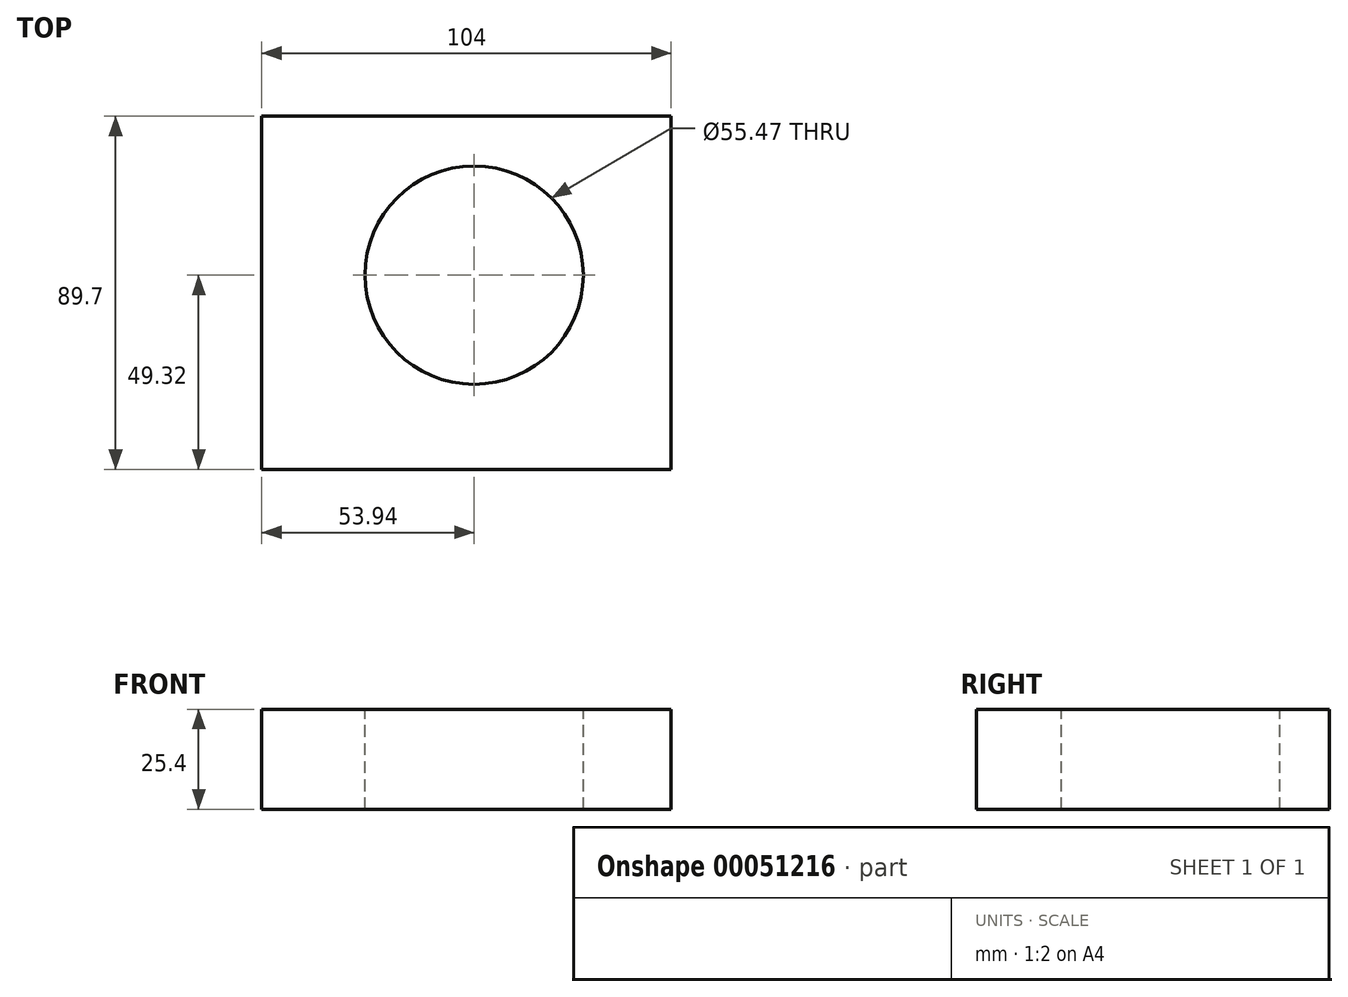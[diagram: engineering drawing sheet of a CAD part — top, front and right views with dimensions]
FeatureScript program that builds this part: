
annotation { "Feature Type Name" : "Feature", "Feature Type Description" : "" }
export const myFeature = defineFeature(function(context is Context, id is Id, definition is map)
    precondition{}
    {
        {
            var Q0;
            Q0=qCreatedBy(makeId("Top.planeOp"),FACE);
            var sketch = newSketch(context, id + "F0", { "sketchPlane" : qUnion([Q0])});
            skLineSegment(sketch, "E0.bottom", {"start": v(-53.94, 40.38) * mm, "end": v(50.06, 40.38) * mm});
            skLineSegment(sketch, "E0.top", {"start": v(-53.94, -49.32) * mm, "end": v(50.06, -49.32) * mm});
            skLineSegment(sketch, "E0.left", {"start": v(-53.94, 40.38) * mm, "end": v(-53.94, -49.32) * mm});
            skLineSegment(sketch, "E0.right", {"start": v(50.06, 40.38) * mm, "end": v(50.06, -49.32) * mm});
            skSolve(sketch);
        }
        {
            var Q0;
            Q0=makeQuery(id+"F0.imprint","IMPRINT",FACE,{"disambiguationData":[TD([[makeQuery(id+"F0.imprint","IMPRINT",EDGE,{"derivedFrom":sQuery(id+"F0.wireOp",EDGE,"E0.bottom")}),-1.0]])]});
            extrude(context, id + "F1", {"entities" : qUnion([Q0]), "depth" : 25.4 * mm});
        }
        {
            var Q0;
            Q0=makeQuery(id+"F1.opExtrude","CAP_FACE",FACE,{"disambiguationData":[OSD([sQuery(id+"F0.wireOp",EDGE,"E0.bottom"),sQuery(id+"F0.wireOp",EDGE,"E0.top"),sQuery(id+"F0.wireOp",EDGE,"E0.left"),sQuery(id+"F0.wireOp",EDGE,"E0.right")])],"isStart":false});
            var sketch = newSketch(context, id + "F2", { "sketchPlane" : qUnion([Q0])});
            skCircle(sketch, "E1", {"center": v(0, 0) * mm, "radius": 27.73 * mm});
            skSolve(sketch);
        }
        {
            var Q0;
            Q0 = qSketchRegion(id + "F2", true);
            extrude(context, id + "F3", {"entities" : qUnion([Q0]), "operationType" : NewBodyOperationType.REMOVE, "oppositeDirection" : true, "depth" : 25.4 * mm});
        }
    });
